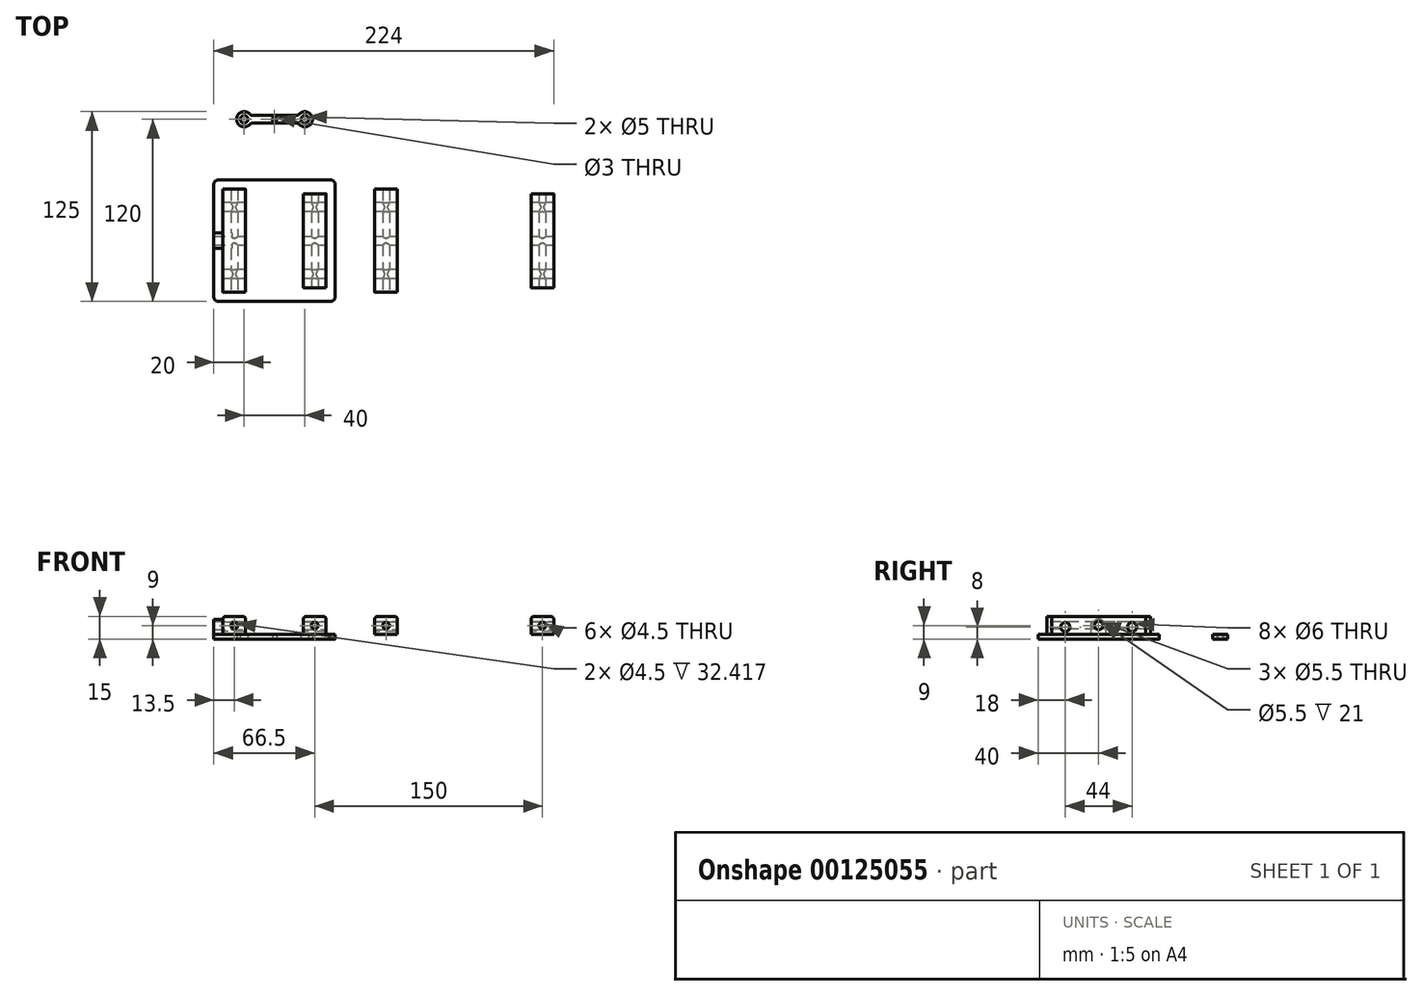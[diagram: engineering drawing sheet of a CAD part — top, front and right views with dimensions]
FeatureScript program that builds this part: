
annotation { "Feature Type Name" : "Feature", "Feature Type Description" : "" }
export const myFeature = defineFeature(function(context is Context, id is Id, definition is map)
    precondition{}
    {
        {
            assignVariable(context, id + "F0", {"name" : "e", "anyValue" : 3});
        }
        {
            assignVariable(context, id + "F1", {"name" : "c", "anyValue" : 15});
        }
        {
            var Q0;
            Q0=qCreatedBy(makeId("Top.planeOp"),FACE);
            var sketch = newSketch(context, id + "F2", { "sketchPlane" : qUnion([Q0])});
            skLineSegment(sketch, "E0.bottom", {"start": v(37, 40) * mm, "end": v(-37, 40) * mm});
            skLineSegment(sketch, "E0.top", {"start": v(37, -40) * mm, "end": v(-37, -40) * mm});
            skLineSegment(sketch, "E0.left", {"start": v(40, 37) * mm, "end": v(40, -37) * mm});
            skLineSegment(sketch, "E0.right", {"start": v(-40, 37) * mm, "end": v(-40, -37) * mm});
            skPoint(sketch, "E0.middle", {"position": v(0, 0) * mm});
            skPoint(sketch, "E1.visualSharp", {"position": v(40, 40) * mm});
            skArc(sketch, "E1.filletArc", {"start": v(40, 37) * mm, "mid": v(39.12, 39.12) * mm, "end": v(37, 40) * mm});
            skPoint(sketch, "E2.visualSharp", {"position": v(40, -40) * mm});
            skArc(sketch, "E2.filletArc", {"start": v(37, -40) * mm, "mid": v(39.12, -39.12) * mm, "end": v(40, -37) * mm});
            skPoint(sketch, "E3.visualSharp", {"position": v(-40, -40) * mm});
            skArc(sketch, "E3.filletArc", {"start": v(-40, -37) * mm, "mid": v(-39.12, -39.12) * mm, "end": v(-37, -40) * mm});
            skPoint(sketch, "E4.visualSharp", {"position": v(-40, 40) * mm});
            skArc(sketch, "E4.filletArc", {"start": v(-37, 40) * mm, "mid": v(-39.12, 39.12) * mm, "end": v(-40, 37) * mm});
            skSolve(sketch);
        }
        {
            var Q0;
            Q0=makeQuery(id+"F2.imprint","IMPRINT",FACE,{"disambiguationData":[TD([[makeQuery(id+"F2.imprint","IMPRINT",EDGE,{"derivedFrom":sQuery(id+"F2.wireOp",EDGE,"E0.bottom")}),1.0]])]});
            extrude(context, id + "F3", {"entities" : qUnion([Q0]), "depth" : (getVariable(context, 'e')) * mm});
        }
        {
            var Q0;
            Q0=makeQuery(id+"F3.opExtrude","CAP_FACE",FACE,{"disambiguationData":[OSD([sQuery(id+"F2.wireOp",EDGE,"E0.bottom"),sQuery(id+"F2.wireOp",EDGE,"E0.top"),sQuery(id+"F2.wireOp",EDGE,"E0.left"),sQuery(id+"F2.wireOp",EDGE,"E0.right")])],"isStart":false});
            var sketch = newSketch(context, id + "F4", { "sketchPlane" : qUnion([Q0])});
            skLineSegment(sketch, "E5", {"start": v(-40, 0) * mm, "end": v(40, 0) * mm, "construction": true});
            skLineSegment(sketch, "E6.bottom", {"start": v(-19, 34) * mm, "end": v(-34, 34) * mm});
            skLineSegment(sketch, "E6.top", {"start": v(-19, -34) * mm, "end": v(-34, -34) * mm});
            skLineSegment(sketch, "E6.left", {"start": v(-19, 34) * mm, "end": v(-19, -34) * mm});
            skLineSegment(sketch, "E6.right", {"start": v(-34, 34) * mm, "end": v(-34, -34) * mm});
            skPoint(sketch, "E6.middle", {"position": v(-26.5, 0) * mm});
            skLineSegment(sketch, "E7.bottom", {"start": v(34, 31) * mm, "end": v(19, 31) * mm});
            skLineSegment(sketch, "E7.top", {"start": v(34, -31) * mm, "end": v(19, -31) * mm});
            skLineSegment(sketch, "E7.left", {"start": v(34, 31) * mm, "end": v(34, -31) * mm});
            skLineSegment(sketch, "E7.right", {"start": v(19, 31) * mm, "end": v(19, -31) * mm});
            skPoint(sketch, "E7.middle", {"position": v(26.5, 0) * mm});
            skSolve(sketch);
        }
        {
            var Q0;
            Q0 = qSketchRegion(id + "F4", true);
            extrude(context, id + "F5", {"entities" : qUnion([Q0]), "depth" : (getVariable(context, 'c') - getVariable(context, 'e')) * mm});
        }
        {
            var Q0;
            Q0=makeQuery(id+"F5.opExtrude","SWEPT_FACE",FACE,{"disambiguationData":[OSD([sQuery(id+"F4.wireOp",EDGE,"E6.top")])]});
            var sketch = newSketch(context, id + "F6", { "sketchPlane" : qUnion([Q0])});
            skLineSegment(sketch, "E8", {"start": v(-34, 9) * mm, "end": v(-19, 9) * mm, "construction": true});
            skLineSegment(sketch, "E9", {"start": v(-26.5, 15) * mm, "end": v(-26.5, 3) * mm, "construction": true});
            skCircle(sketch, "E10", {"center": v(-26.5, 9) * mm, "radius": 2.25 * mm});
            skSolve(sketch);
        }
        {
            var Q0;
            Q0=makeQuery(id+"F5.opExtrude","SWEPT_FACE",FACE,{"disambiguationData":[OSD([sQuery(id+"F4.wireOp",EDGE,"E7.top")])]});
            var sketch = newSketch(context, id + "F7", { "sketchPlane" : qUnion([Q0])});
            skLineSegment(sketch, "E11", {"start": v(19, 9) * mm, "end": v(34, 9) * mm, "construction": true});
            skLineSegment(sketch, "E12", {"start": v(26.5, 15) * mm, "end": v(26.5, 3) * mm, "construction": true});
            skCircle(sketch, "E13", {"center": v(26.5, 9) * mm, "radius": 2.25 * mm});
            skSolve(sketch);
        }
        {
            var Q0;
            Q0 = qSketchRegion(id + "F6", true);
            extrude(context, id + "F8", {"entities" : qUnion([Q0]), "operationType" : NewBodyOperationType.REMOVE, "endBound" : BoundingType.THROUGH_ALL, "oppositeDirection" : true, "depth" : 25 * mm});
        }
        {
            var Q0;
            Q0 = qSketchRegion(id + "F7", true);
            extrude(context, id + "F9", {"entities" : qUnion([Q0]), "operationType" : NewBodyOperationType.REMOVE, "endBound" : BoundingType.THROUGH_ALL, "oppositeDirection" : true, "depth" : 25 * mm});
        }
        {
            var Q0;
            Q0=makeQuery(id+"F5.opExtrude","SWEPT_FACE",FACE,{"disambiguationData":[OSD([sQuery(id+"F4.wireOp",EDGE,"E7.left")])]});
            var sketch = newSketch(context, id + "F10", { "sketchPlane" : qUnion([Q0])});
            skLineSegment(sketch, "E14", {"start": v(-31, 9) * mm, "end": v(31, 9) * mm, "construction": true});
            skCircle(sketch, "E15", {"center": v(0, 9) * mm, "radius": 2.75 * mm});
            skSolve(sketch);
        }
        {
            var Q0;
            Q0 = qSketchRegion(id + "F10", true);
            extrude(context, id + "F11", {"entities" : qUnion([Q0]), "operationType" : NewBodyOperationType.REMOVE, "endBound" : BoundingType.THROUGH_ALL, "oppositeDirection" : true, "depth" : 25 * mm});
        }
        {
            var Q0;
            Q0=makeQuery(id+"F5.opExtrude","CAP_EDGE",EDGE,{"disambiguationData":[OSD([sQuery(id+"F4.wireOp",EDGE,"E7.right")])],"isStart":false});
            var Q1;
            Q1=makeQuery(id+"F5.opExtrude","CAP_EDGE",EDGE,{"disambiguationData":[OSD([sQuery(id+"F4.wireOp",EDGE,"E7.left")])],"isStart":false});
            var Q2;
            Q2=makeQuery(id+"F5.opExtrude","CAP_EDGE",EDGE,{"disambiguationData":[OSD([sQuery(id+"F4.wireOp",EDGE,"E6.left")])],"isStart":false});
            var Q3;
            Q3=makeQuery(id+"F5.opExtrude","CAP_EDGE",EDGE,{"disambiguationData":[OSD([sQuery(id+"F4.wireOp",EDGE,"E6.right")])],"isStart":false});
            fillet(context, id + "F12", {"entities" : qUnion([Q0, Q1, Q2, Q3]), "radius" : 2 * mm, "tangentPropagation" : true, "allowEdgeOverflow" : false});
        }
        {
            var Q0;
            Q0=qCreatedBy(makeId("Top.planeOp"),FACE);
            var sketch = newSketch(context, id + "F13", { "sketchPlane" : qUnion([Q0])});
            skLineSegment(sketch, "E16.bottom", {"start": v(-14.2, 77.5) * mm, "end": v(14.2, 77.5) * mm});
            skLineSegment(sketch, "E16.top", {"start": v(-14.2, 82.5) * mm, "end": v(14.2, 82.5) * mm});
            skPoint(sketch, "E16.middle", {"position": v(0, 80) * mm});
            skCircle(sketch, "E17", {"center": v(20, 80) * mm, "radius": 2.5 * mm});
            skCircle(sketch, "E18", {"center": v(-20, 80) * mm, "radius": 2.5 * mm});
            skArc(sketch, "E19", {"start": v(16.37, 76.56) * mm, "mid": v(25, 80) * mm, "end": v(16.37, 83.44) * mm});
            skArc(sketch, "E20", {"start": v(-16.37, 83.44) * mm, "mid": v(-25, 80) * mm, "end": v(-16.37, 76.56) * mm});
            skPoint(sketch, "E21.orphan", {"position": v(20, 82.5) * mm});
            skPoint(sketch, "E16.right.start.orphan", {"position": v(20, 77.5) * mm});
            skPoint(sketch, "E22.orphan", {"position": v(-20, 82.5) * mm});
            skPoint(sketch, "E16.left.start.orphan", {"position": v(-20, 77.5) * mm});
            skPoint(sketch, "E23.visualSharp", {"position": v(15.67, 77.5) * mm});
            skArc(sketch, "E23.filletArc", {"start": v(16.37, 76.56) * mm, "mid": v(15.38, 77.26) * mm, "end": v(14.2, 77.5) * mm});
            skPoint(sketch, "E24.visualSharp", {"position": v(15.67, 82.5) * mm});
            skArc(sketch, "E24.filletArc", {"start": v(14.2, 82.5) * mm, "mid": v(15.38, 82.74) * mm, "end": v(16.37, 83.44) * mm});
            skPoint(sketch, "E25.visualSharp", {"position": v(-15.67, 82.5) * mm});
            skArc(sketch, "E25.filletArc", {"start": v(-16.37, 83.44) * mm, "mid": v(-15.38, 82.74) * mm, "end": v(-14.2, 82.5) * mm});
            skPoint(sketch, "E26.visualSharp", {"position": v(-15.67, 77.5) * mm});
            skArc(sketch, "E26.filletArc", {"start": v(-14.2, 77.5) * mm, "mid": v(-15.38, 77.26) * mm, "end": v(-16.37, 76.56) * mm});
            skCircle(sketch, "E27", {"center": v(0, 80) * mm, "radius": 1.5 * mm});
            skSolve(sketch);
        }
        {
            var Q0;
            Q0 = qSketchRegion(id + "F13", true);
            extrude(context, id + "F14", {"entities" : qUnion([Q0]), "depth" : (getVariable(context, 'e')) * mm});
        }
        {
            var Q0;
            Q0=makeQuery(id+"F5.opExtrude","SWEPT_BODY",BODY,{"disambiguationData":[OSD([sQuery(id+"F4.wireOp",EDGE,"E6.bottom"),sQuery(id+"F4.wireOp",EDGE,"E6.top"),sQuery(id+"F4.wireOp",EDGE,"E6.left"),sQuery(id+"F4.wireOp",EDGE,"E6.right")])]});
            transform(context, id + "F15", {"entities" : qUnion([Q0]), "transformType" : TransformType.TRANSLATION_3D, "dx" : 100 * mm, "dy" : 0 * mm, "dz" : 0 * mm, "makeCopy" : true});
        }
        {
            var Q0;
            Q0=makeQuery(id+"F5.opExtrude","SWEPT_BODY",BODY,{"disambiguationData":[OSD([sQuery(id+"F4.wireOp",EDGE,"E7.bottom"),sQuery(id+"F4.wireOp",EDGE,"E7.top"),sQuery(id+"F4.wireOp",EDGE,"E7.left"),sQuery(id+"F4.wireOp",EDGE,"E7.right")])]});
            transform(context, id + "F16", {"entities" : qUnion([Q0]), "transformType" : TransformType.TRANSLATION_3D, "dx" : 150 * mm, "dy" : 0 * mm, "dz" : 0 * mm, "makeCopy" : true});
        }
        {
            var Q0;
            Q0=makeQuery(id+"F5.opExtrude","SWEPT_FACE",FACE,{"disambiguationData":[OSD([sQuery(id+"F4.wireOp",EDGE,"E7.left")])]});
            var sketch = newSketch(context, id + "F17", { "sketchPlane" : qUnion([Q0])});
            skLineSegment(sketch, "E28", {"start": v(-31, 8) * mm, "end": v(31, 8) * mm, "construction": true});
            skCircle(sketch, "E29", {"center": v(-22, 8) * mm, "radius": 3 * mm});
            skCircle(sketch, "E30.MirrorC", {"center": v(22, 8) * mm, "radius": 3 * mm});
            skLineSegment(sketch, "E31.MirrorCS", {"start": v(31, 8) * mm, "end": v(-31, 8) * mm, "construction": true});
            skSolve(sketch);
        }
        {
            var Q0;
            Q0 = qSketchRegion(id + "F17", true);
            extrude(context, id + "F18", {"entities" : qUnion([Q0]), "operationType" : NewBodyOperationType.REMOVE, "endBound" : BoundingType.SYMMETRIC, "depth" : 300 * mm});
        }
        {
            var Q0;
            Q0=makeQuery(id+"F5.opExtrude","SWEPT_FACE",FACE,{"disambiguationData":[OSD([sQuery(id+"F4.wireOp",EDGE,"E6.right")])]});
            var sketch = newSketch(context, id + "F19", { "sketchPlane" : qUnion([Q0])});
            skLineSegment(sketch, "E32.bottom", {"start": v(-5, 3) * mm, "end": v(5, 3) * mm});
            skLineSegment(sketch, "E32.top", {"start": v(-5, 15) * mm, "end": v(5, 15) * mm});
            skLineSegment(sketch, "E32.left", {"start": v(-5, 3) * mm, "end": v(-5, 15) * mm});
            skLineSegment(sketch, "E32.right", {"start": v(5, 3) * mm, "end": v(5, 15) * mm});
            skPoint(sketch, "E32.middle", {"position": v(0, 9) * mm});
            skSolve(sketch);
        }
        {
            var Q0;
            {var subQ3=sQuery(id+"F19.wireOp",EDGE,"E32.bottom");Q0=makeQuery(id+"F19.imprint","IMPRINT",FACE,{"disambiguationData":[TD([[makeQuery(id+"F19.imprint","IMPRINT",EDGE,{"derivedFrom":subQ3}),1.0]])]});}
            extrude(context, id + "F20", {"entities" : qUnion([Q0]), "operationType" : NewBodyOperationType.ADD, "endBound" : BoundingType.SYMMETRIC, "depth" : 12 * mm});
        }
        {
            var Q0;
            Q0=makeQuery(id+"F20.opExtrude","SWEPT_EDGE",EDGE,{"disambiguationData":[OSD([sQuery(id+"F4.wireOp",EDGE,"E6.right"),sQuery(id+"F19.wireOp",EDGE,"E32.right")])]});
            var Q1;
            Q1=makeQuery(id+"F20.opExtrude","SWEPT_EDGE",EDGE,{"disambiguationData":[OSD([sQuery(id+"F4.wireOp",EDGE,"E6.right"),sQuery(id+"F19.wireOp",EDGE,"E32.left")])]});
            fillet(context, id + "F21", {"entities" : qUnion([Q0, Q1]), "radius" : 5 * mm, "tangentPropagation" : true, "allowEdgeOverflow" : false});
        }
    });
